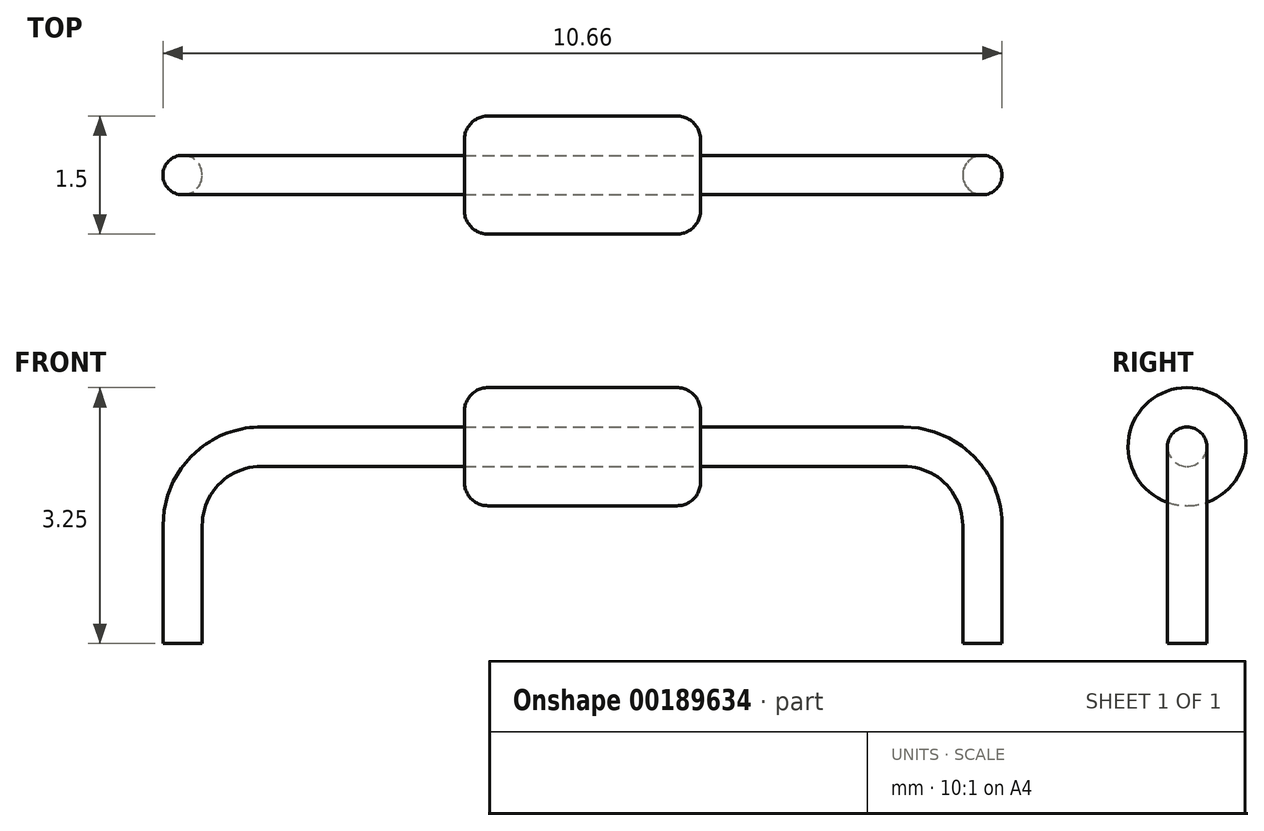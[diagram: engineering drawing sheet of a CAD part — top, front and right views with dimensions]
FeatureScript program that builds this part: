
annotation { "Feature Type Name" : "Feature", "Feature Type Description" : "" }
export const myFeature = defineFeature(function(context is Context, id is Id, definition is map)
    precondition{}
    {
        {
            var Q0;
            Q0=qCreatedBy(makeId("Right.planeOp"),FACE);
            var sketch = newSketch(context, id + "F0", { "sketchPlane" : qUnion([Q0])});
            skCircle(sketch, "E0", {"center": v(0, 0) * mm, "radius": 0.75 * mm});
            skSolve(sketch);
        }
        {
            var Q0;
            Q0 = qSketchRegion(id + "F0", true);
            extrude(context, id + "F1", {"entities" : qUnion([Q0]), "depth" : 3 * mm, "symmetric" : true});
        }
        {
            var Q0;
            Q0=makeQuery(id+"F1.opExtrude","CAP_EDGE",EDGE,{"disambiguationData":[OSD([sQuery(id+"F0.wireOp",EDGE,"E0")])],"isStart":true});
            var Q1;
            Q1=makeQuery(id+"F1.opExtrude","CAP_EDGE",EDGE,{"disambiguationData":[OSD([sQuery(id+"F0.wireOp",EDGE,"E0")])],"isStart":false});
            fillet(context, id + "F2", {"entities" : qUnion([Q0, Q1]), "radius" : 0.3 * mm, "tangentPropagation" : true, "allowEdgeOverflow" : false});
        }
        {
            var Q0;
            Q0=qCreatedBy(makeId("Front.planeOp"),FACE);
            var sketch = newSketch(context, id + "F3", { "sketchPlane" : qUnion([Q0])});
            skLineSegment(sketch, "E1", {"start": v(-5.08, -2.5) * mm, "end": v(-5.08, -1) * mm});
            skLineSegment(sketch, "E2", {"start": v(-4.08, 0) * mm, "end": v(4.08, 0) * mm});
            skLineSegment(sketch, "E3", {"start": v(5.08, -1) * mm, "end": v(5.08, -2.5) * mm});
            skPoint(sketch, "E4.visualSharp", {"position": v(-5.08, 0) * mm});
            skArc(sketch, "E4.filletArc", {"start": v(-4.08, 0) * mm, "mid": v(-4.79, -0.3) * mm, "end": v(-5.08, -1) * mm});
            skPoint(sketch, "E5.visualSharp", {"position": v(5.08, 0) * mm});
            skArc(sketch, "E5.filletArc", {"start": v(5.08, -1) * mm, "mid": v(4.79, -0.3) * mm, "end": v(4.08, 0) * mm});
            skPoint(sketch, "E6", {"position": v(0, 0) * mm});
            skSolve(sketch);
        }
        {
            var Q0;
            Q0=sQuery(id+"F3.wireOp",EDGE,"E1");
            var Q1;
            Q1=sQuery(id+"F3.wireOp",VERTEX,"E1.start");
            cPlane(context, id + "F4", {"entities" : qUnion([Q0, Q1]), "cplaneType" : CPlaneType.CURVE_POINT, "offset" : 25 * mm, "width" : 150 * mm, "height" : 150 * mm});
        }
        {
            var Q0;
            Q0=qCreatedBy(id+"F4.planeOp",FACE);
            var sketch = newSketch(context, id + "F5", { "sketchPlane" : qUnion([Q0])});
            skCircle(sketch, "E7", {"center": v(-5.08, 0) * mm, "radius": 0.25 * mm});
            skSolve(sketch);
        }
        {
            var Q0;
            Q0 = qSketchRegion(id + "F5", true);
            var Q1;
            Q1 = qConstructionFilter(qBodyType(qCreatedBy(id + "F3" ,EDGE), BodyType.WIRE), ConstructionObject.NO);
            sweep(context, id + "F6", {"profiles" : qUnion([Q0]), "path" : qUnion([Q1])});
        }
    });
